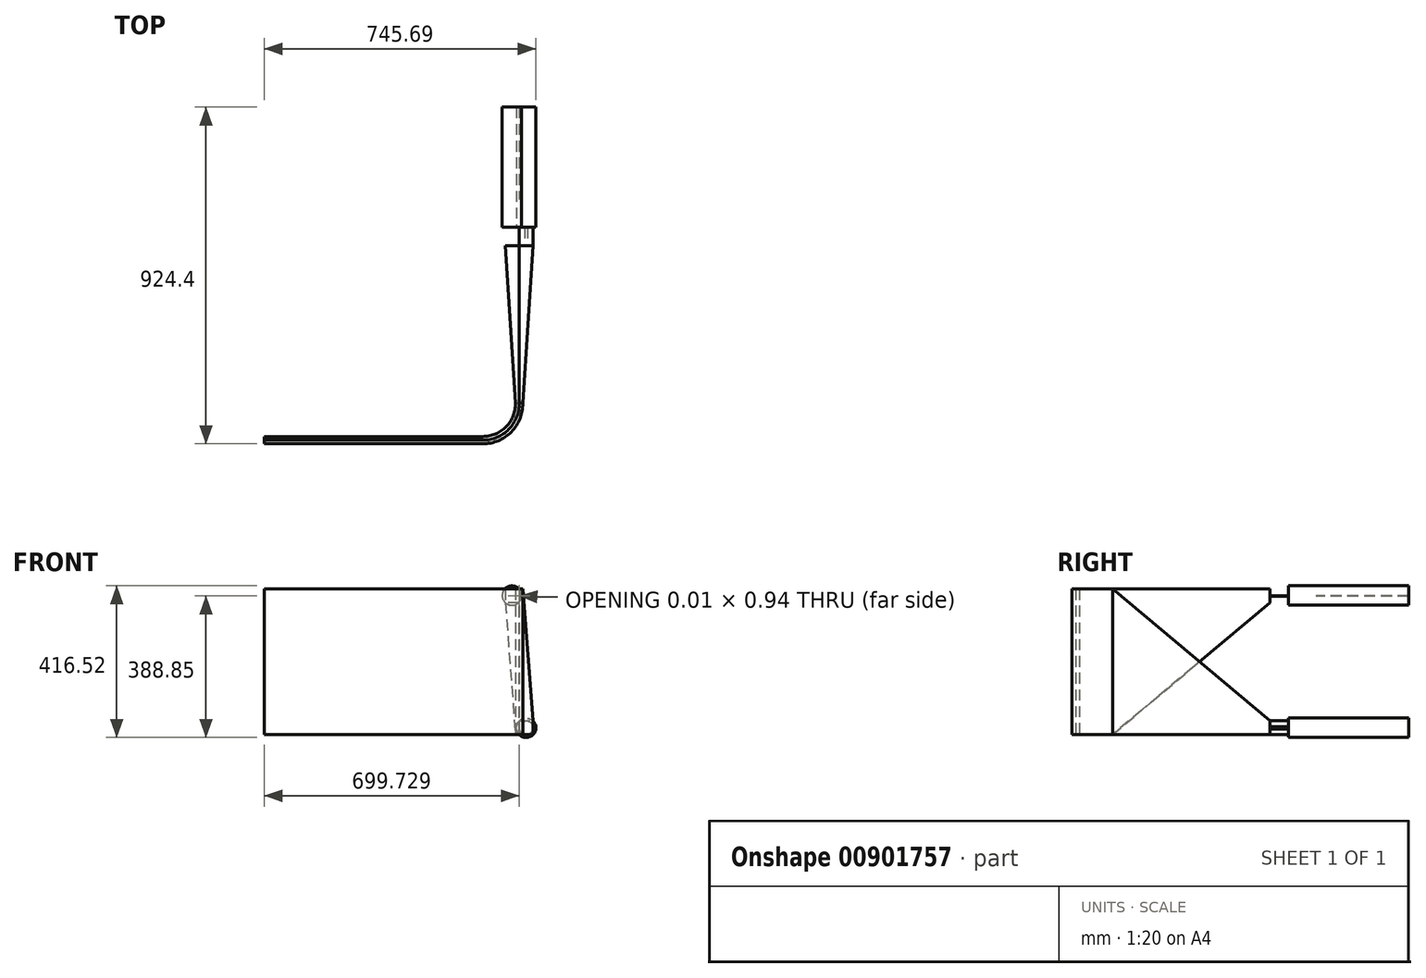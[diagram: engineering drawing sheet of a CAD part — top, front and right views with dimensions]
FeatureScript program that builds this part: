
annotation { "Feature Type Name" : "Feature", "Feature Type Description" : "" }
export const myFeature = defineFeature(function(context is Context, id is Id, definition is map)
    precondition{}
    {
        {
            var Q0;
            Q0=qCreatedBy(makeId("Top.planeOp"),FACE);
            var sketch = newSketch(context, id + "F0", { "sketchPlane" : qUnion([Q0])});
            skLineSegment(sketch, "E0", {"start": v(0, 0) * mm, "end": v(600, 0) * mm});
            skLineSegment(sketch, "E1", {"start": v(0, 0) * mm, "end": v(0, 10) * mm});
            skLineSegment(sketch, "E2", {"start": v(0, 10) * mm, "end": v(600, 10) * mm});
            skLineSegment(sketch, "E3", {"start": v(600, 10) * mm, "end": v(600, 0) * mm});
            skArc(sketch, "E4", {"start": v(600, 10) * mm, "mid": v(664.11, 36.94) * mm, "end": v(689.73, 101.6) * mm});
            skLineSegment(sketch, "E5", {"start": v(689.73, 101.6) * mm, "end": v(699.73, 101.6) * mm});
            skArc(sketch, "E6", {"start": v(600, 0) * mm, "mid": v(671.18, 29.87) * mm, "end": v(699.73, 101.6) * mm});
            skLineSegment(sketch, "E7", {"start": v(689.73, 101.6) * mm, "end": v(689.73, 533.4) * mm});
            skLineSegment(sketch, "E8", {"start": v(689.73, 533.4) * mm, "end": v(699.73, 533.4) * mm});
            skLineSegment(sketch, "E9", {"start": v(699.73, 533.4) * mm, "end": v(699.73, 101.6) * mm});
            skSolve(sketch);
        }
        {
            var Q0;
            Q0=qCreatedBy(makeId("Top.planeOp"),FACE);
            var sketch = newSketch(context, id + "F1", { "sketchPlane" : qUnion([Q0])});
            skLineSegment(sketch, "E10.bottom", {"start": v(0, 0) * mm, "end": v(600, 0) * mm});
            skLineSegment(sketch, "E10.top", {"start": v(0, -10) * mm, "end": v(600, -10) * mm});
            skLineSegment(sketch, "E10.left", {"start": v(0, 0) * mm, "end": v(0, -10) * mm});
            skLineSegment(sketch, "E10.right", {"start": v(600, 0) * mm, "end": v(600, -10) * mm});
            skLineSegment(sketch, "E11", {"start": v(699.72, 101.6) * mm, "end": v(709.72, 101.6) * mm});
            skArc(sketch, "E12", {"start": v(600, -10) * mm, "mid": v(678.25, 22.8) * mm, "end": v(709.72, 101.6) * mm});
            skLineSegment(sketch, "E13", {"start": v(709.72, 533.4) * mm, "end": v(709.72, 101.6) * mm});
            skArc(sketch, "E14", {"start": v(600, 0) * mm, "mid": v(671.18, 29.87) * mm, "end": v(699.72, 101.6) * mm});
            skLineSegment(sketch, "E15", {"start": v(699.72, 101.6) * mm, "end": v(699.72, 533.4) * mm});
            skLineSegment(sketch, "E16", {"start": v(709.72, 533.4) * mm, "end": v(699.72, 533.4) * mm});
            skSolve(sketch);
        }
        {
            var Q0;
            Q0=makeQuery(id+"F0.imprint","IMPRINT",FACE,{"disambiguationData":[TD([[makeQuery(id+"F0.imprint","IMPRINT",EDGE,{"derivedFrom":sQuery(id+"F0.wireOp",EDGE,"E3")}),1.0]])]});
            var Q1;
            Q1=makeQuery(id+"F0.imprint","IMPRINT",FACE,{"disambiguationData":[TD([[makeQuery(id+"F0.imprint","IMPRINT",EDGE,{"derivedFrom":sQuery(id+"F0.wireOp",EDGE,"E0")}),1.0]])]});
            var Q2;
            Q2=makeQuery(id+"F1.imprint","IMPRINT",FACE,{"disambiguationData":[TD([[makeQuery(id+"F1.imprint","IMPRINT",EDGE,{"derivedFrom":sQuery(id+"F1.wireOp",EDGE,"E10.right")}),1.0]])]});
            var Q3;
            Q3=makeQuery(id+"F1.imprint","IMPRINT",FACE,{"disambiguationData":[TD([[makeQuery(id+"F1.imprint","IMPRINT",EDGE,{"derivedFrom":sQuery(id+"F1.wireOp",EDGE,"E10.bottom")}),-1.0]])]});
            var Q4;
            Q4=makeQuery(id+"F1.imprint","IMPRINT",FACE,{"disambiguationData":[TD([[makeQuery(id+"F1.imprint","IMPRINT",EDGE,{"derivedFrom":sQuery(id+"F1.wireOp",EDGE,"X5Z3EWSr-kG4Y-lZXF-lFXy-ctdBk5cdvKgP.top")}),-1.0]])]});
            var Q5;
            Q5=makeQuery(id+"F0.imprint","IMPRINT",FACE,{"disambiguationData":[TD([[makeQuery(id+"F0.imprint","IMPRINT",EDGE,{"derivedFrom":sQuery(id+"F0.wireOp",EDGE,"E5")}),1.0]])]});
            var Q6;
            Q6=makeQuery(id+"F1.imprint","IMPRINT",FACE,{"disambiguationData":[TD([[makeQuery(id+"F1.imprint","IMPRINT",EDGE,{"derivedFrom":sQuery(id+"F1.wireOp",EDGE,"E11")}),1.0]])]});
            extrude(context, id + "F2", {"entities" : qUnion([Q0, Q1, Q2, Q3, Q4, Q5, Q6]), "depth" : 400 * mm, "offsetDistance" : 25.4 * mm});
        }
        {
            var Q0;
            Q0=makeQuery(id+"F2.opExtrude","CAP_EDGE",EDGE,{"disambiguationData":[OSD([sQuery(id+"F0.wireOp",EDGE,"E8")])],"isStart":true});
            var Q1;
            Q1=makeQuery(id+"F2.opExtrude","CAP_EDGE",EDGE,{"disambiguationData":[OSD([sQuery(id+"F1.wireOp",EDGE,"E16")])],"isStart":false});
            chamfer(context, id + "F3", {"entities" : qUnion([Q0, Q1]), "chamferType" : ChamferType.TWO_OFFSETS, "width1" : 431.8 * mm, "oppositeDirection" : false, "width2" : 362.2 * mm, "tangentPropagation" : true});
        }
        {
            var Q0;
            Q0=makeQuery(id+"F2.opExtrude","SWEPT_FACE",FACE,{"disambiguationData":[OSD([sQuery(id+"F1.wireOp",EDGE,"E13")])]});
            extrude(context, id + "F4", {"entities" : qUnion([Q0]), "operationType" : NewBodyOperationType.ADD, "depth" : 28.02 * mm, "offsetDistance" : 25.4 * mm});
        }
        {
            var Q0;
            Q0=makeQuery(id+"F2.opExtrude","SWEPT_FACE",FACE,{"disambiguationData":[OSD([sQuery(id+"F0.wireOp",EDGE,"E7")])]});
            extrude(context, id + "F5", {"entities" : qUnion([Q0]), "operationType" : NewBodyOperationType.ADD, "depth" : 28.02 * mm, "offsetDistance" : 25.4 * mm});
        }
        {
            var Q0;
            {var subQ0=sQuery(id+"F1.wireOp",EDGE,"E16");var subQ1=sQuery(id+"F1.wireOp",EDGE,"E13");Q0=makeQuery(id+"F4.boolean.opBoolean","MERGE",FACE,{"derivedFrom":[makeQuery(id+"F2.opExtrude","SWEPT_FACE",FACE,{"disambiguationData":[OSD([subQ0])]}),makeQuery(id+"F4.opExtrude","SWEPT_FACE",FACE,{"disambiguationData":[OSD([subQ1,subQ0]),TDD([makeQuery(id+"F2.opExtrude","SWEPT_EDGE",EDGE,{"disambiguationData":[OSD([subQ1,subQ0])]})])]})]});}
            var sketch = newSketch(context, id + "F6", { "sketchPlane" : qUnion([Q0])});
            skCircle(sketch, "E17", {"center": v(-719.02, 18.72) * mm, "radius": 19.05 * mm});
            skSolve(sketch);
        }
        {
            var Q0;
            {var subQ0=sQuery(id+"F6.wireOp",EDGE,"E17");var subQ1=sQuery(id+"F1.wireOp",EDGE,"E16");var subQ2=sQuery(id+"F1.wireOp",EDGE,"E13");var subQ3=makeQuery(id+"F4.opExtrude","CAP_EDGE",EDGE,{"disambiguationData":[OSD([subQ2,subQ1]),TDD([makeQuery(id+"F2.opExtrude","SWEPT_EDGE",EDGE,{"disambiguationData":[OSD([subQ2,subQ1])]})])],"isStart":false});var subQ4=makeQuery(id+"F6.imprint","INTERSECT",VERTEX,{"disambiguationData":[OD(0.0)],"derivedFrom":[subQ3,subQ0]});Q0=makeQuery(id+"F6.imprint","IMPRINT",FACE,{"disambiguationData":[TD([[makeQuery(id+"F6.imprint","IMPRINT",EDGE,{"disambiguationData":[TD([[subQ4,-1.0]])],"derivedFrom":subQ0}),1.0]])]});}
            extrude(context, id + "F7", {"entities" : qUnion([Q0]), "operationType" : NewBodyOperationType.ADD, "depth" : 127 * mm, "offsetDistance" : 25.4 * mm});
        }
        {
            var Q0;
            {var subQ0=sQuery(id+"F0.wireOp",EDGE,"E8");var subQ1=sQuery(id+"F0.wireOp",EDGE,"E7");Q0=makeQuery(id+"F5.boolean.opBoolean","MERGE",FACE,{"derivedFrom":[makeQuery(id+"F2.opExtrude","SWEPT_FACE",FACE,{"disambiguationData":[OSD([subQ0])]}),makeQuery(id+"F5.opExtrude","SWEPT_FACE",FACE,{"disambiguationData":[OSD([subQ1,subQ0]),TDD([makeQuery(id+"F2.opExtrude","SWEPT_EDGE",EDGE,{"disambiguationData":[OSD([subQ1,subQ0])]})])]})]});}
            var sketch = newSketch(context, id + "F8", { "sketchPlane" : qUnion([Q0])});
            skCircle(sketch, "E18", {"center": v(-680.68, 380.9) * mm, "radius": 19.05 * mm});
            skSolve(sketch);
        }
        {
            var Q0;
            {var subQ0=sQuery(id+"F8.wireOp",EDGE,"E18");var subQ1=sQuery(id+"F0.wireOp",EDGE,"E8");var subQ2=makeQuery(id+"F2.opExtrude","SWEPT_EDGE",EDGE,{"disambiguationData":[OSD([subQ1,sQuery(id+"F0.wireOp",EDGE,"E9")])]});var subQ3=makeQuery(id+"F8.imprint","INTERSECT",VERTEX,{"disambiguationData":[OD(0.0)],"derivedFrom":[subQ2,subQ0]});Q0=makeQuery(id+"F8.imprint","IMPRINT",FACE,{"disambiguationData":[TD([[makeQuery(id+"F8.imprint","IMPRINT",EDGE,{"disambiguationData":[TD([[subQ3,1.0]])],"derivedFrom":subQ0}),1.0]])]});}
            extrude(context, id + "F9", {"entities" : qUnion([Q0]), "operationType" : NewBodyOperationType.ADD, "depth" : 127 * mm, "offsetDistance" : 25.4 * mm});
        }
        {
            var Q0;
            Q0=makeQuery(id+"F7.opExtrude","CAP_FACE",FACE,{"disambiguationData":[OSD([sQuery(id+"F1.wireOp",EDGE,"E13"),sQuery(id+"F1.wireOp",EDGE,"E16"),sQuery(id+"F6.wireOp",EDGE,"E17")])],"isStart":false});
            var sketch = newSketch(context, id + "F10", { "sketchPlane" : qUnion([Q0])});
            skCircle(sketch, "E19", {"center": v(-719.02, 18.72) * mm, "radius": 26.67 * mm});
            skSolve(sketch);
        }
        {
            var Q0;
            Q0=makeQuery(id+"F10.imprint","IMPRINT",FACE,{"disambiguationData":[TD([[makeQuery(id+"F10.imprint","IMPRINT",EDGE,{"derivedFrom":sQuery(id+"F10.wireOp",EDGE,"E19")}),1.0]])]});
            extrude(context, id + "F11", {"entities" : qUnion([Q0]), "operationType" : NewBodyOperationType.ADD, "depth" : 254 * mm, "offsetDistance" : 25.4 * mm, "hasSecondDirection" : true, "secondDirectionOppositeDirection" : true, "secondDirectionDepth" : 76.2 * mm});
        }
        {
            var Q0;
            Q0=makeQuery(id+"F7.opExtrude","CAP_FACE",FACE,{"disambiguationData":[OSD([sQuery(id+"F1.wireOp",EDGE,"E13"),sQuery(id+"F1.wireOp",EDGE,"E16"),sQuery(id+"F6.wireOp",EDGE,"E17")])],"isStart":false});
            extrude(context, id + "F12", {"entities" : qUnion([Q0]), "operationType" : NewBodyOperationType.ADD, "depth" : 254 * mm, "offsetDistance" : 25.4 * mm});
        }
        {
            var Q0;
            Q0=makeQuery(id+"F9.opExtrude","CAP_FACE",FACE,{"disambiguationData":[OSD([sQuery(id+"F0.wireOp",EDGE,"E7"),sQuery(id+"F0.wireOp",EDGE,"E8"),sQuery(id+"F0.wireOp",EDGE,"E9"),sQuery(id+"F8.wireOp",EDGE,"E18")])],"isStart":false});
            var sketch = newSketch(context, id + "F13", { "sketchPlane" : qUnion([Q0])});
            skCircle(sketch, "E20", {"center": v(-679.85, 381.9) * mm, "radius": 26.67 * mm});
            skSolve(sketch);
        }
        {
            var Q0;
            Q0=makeQuery(id+"F13.imprint","IMPRINT",FACE,{"disambiguationData":[TD([[makeQuery(id+"F13.imprint","IMPRINT",EDGE,{"derivedFrom":sQuery(id+"F13.wireOp",EDGE,"E20")}),1.0]])]});
            var Q1;
            {var subQ0=sQuery(id+"F0.wireOp",EDGE,"E9");var subQ1=sQuery(id+"F0.wireOp",EDGE,"E8");Q1=makeQuery(id+"F13.imprint","IMPRINT",FACE,{"disambiguationData":[TD([[makeQuery(id+"F13.imprint","IMPRINT",EDGE,{"derivedFrom":makeQuery(id+"F9.opExtrude","CAP_EDGE",EDGE,{"disambiguationData":[OSD([subQ1,subQ0])],"isStart":false})}),1.0]])]});}
            extrude(context, id + "F14", {"entities" : qUnion([Q0, Q1]), "operationType" : NewBodyOperationType.ADD, "depth" : 254 * mm, "offsetDistance" : 25.4 * mm, "hasSecondDirection" : true, "secondDirectionOppositeDirection" : true, "secondDirectionDepth" : 76.2 * mm});
        }
        {
            var Q0;
            Q0=makeQuery(id+"F4.opExtrude","CAP_EDGE",EDGE,{"disambiguationData":[OSD([sQuery(id+"F1.wireOp",EDGE,"E11"),sQuery(id+"F1.wireOp",EDGE,"E12"),sQuery(id+"F1.wireOp",EDGE,"E13")])],"isStart":false});
            chamfer(context, id + "F15", {"entities" : qUnion([Q0]), "chamferType" : ChamferType.TWO_OFFSETS, "width1" : 431.8 * mm, "oppositeDirection" : false, "width2" : 27.8 * mm, "tangentPropagation" : true});
        }
        {
            var Q0;
            Q0=makeQuery(id+"F5.opExtrude","CAP_EDGE",EDGE,{"disambiguationData":[OSD([sQuery(id+"F0.wireOp",EDGE,"E4"),sQuery(id+"F0.wireOp",EDGE,"E5"),sQuery(id+"F0.wireOp",EDGE,"E7")])],"isStart":false});
            chamfer(context, id + "F16", {"entities" : qUnion([Q0]), "chamferType" : ChamferType.TWO_OFFSETS, "width1" : 27.8 * mm, "oppositeDirection" : false, "width2" : 431.8 * mm, "tangentPropagation" : true});
        }
    });
